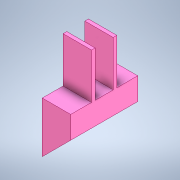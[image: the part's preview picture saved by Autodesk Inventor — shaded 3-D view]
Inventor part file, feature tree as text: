
AUTODESK INVENTOR PART (.ipt)
format: ipt  version: 2022.1 (Build 261234020, 234B)  size: 150,016 bytes
history: native  units: mm
features: extrude x3, sketch x3
ambient origin geometry x8: Origin, YZ Plane, XZ Plane, XY Plane, X Axis, Y Axis, Z Axis, Center Point
bodies: Body1 (feature_tree)
feature tree (6):
  extrude  "Extrusion25"  Depth=150.0mm TaperAngle=0.0deg
  extrude  "Extrusion26"  Depth=8.1mm
  extrude  "Extrusion27"  Depth=40.64mm
  sketch  "Sketch55"  dims[d252=45.0deg d255=150.0mm d256=0.0mm]
  sketch  "Sketch56"  dims[d257=50.0mm d258=0.0mm d259=8.1mm]
  sketch  "Sketch57"  dims[d260=8.1mm d261=40.64mm d262=101.6mm d263=0.0mm d64=1.0mm d65=1.0mm d66=1.0mm d67=0.15mm d68=0.25mm d69=0.375mm d70=14.3117mm d71=0.75mm d72=20.594885mm d73=0.0625mm d74=0.75mm d75=0.375mm]
